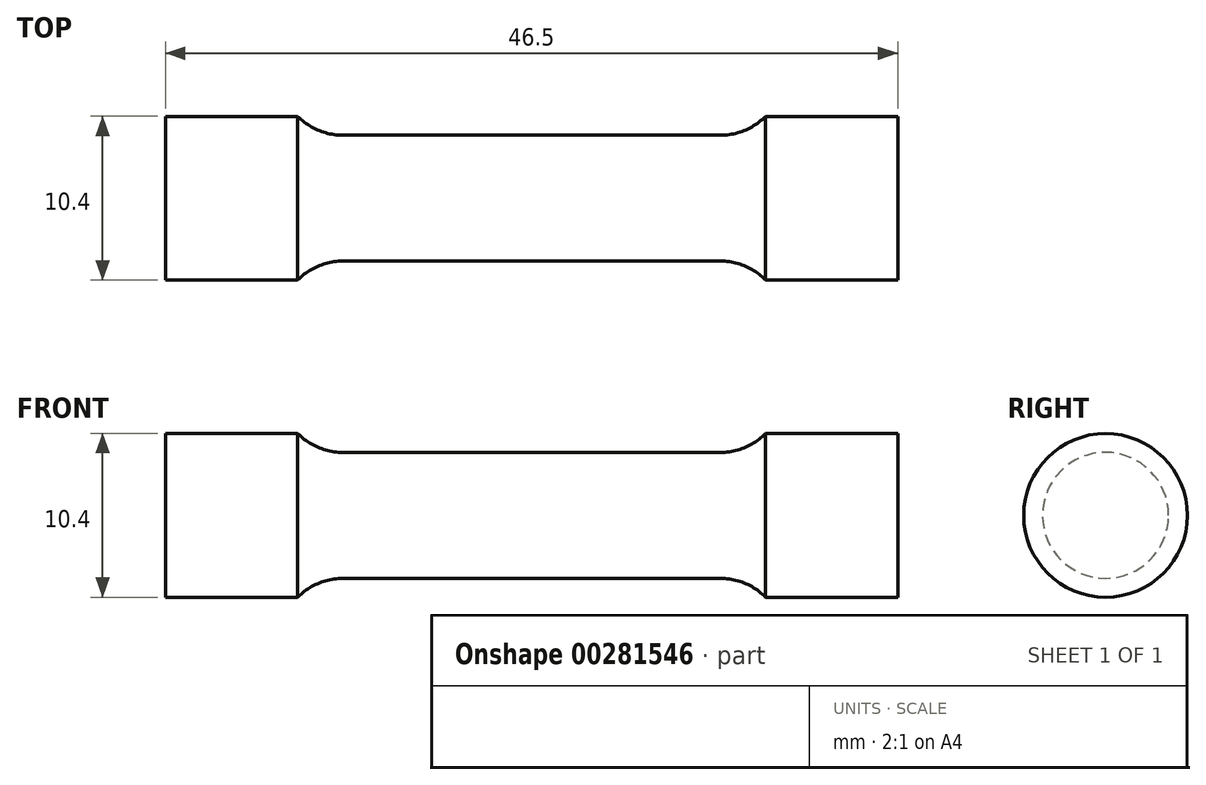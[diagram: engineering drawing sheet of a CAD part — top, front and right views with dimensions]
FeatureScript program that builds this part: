
annotation { "Feature Type Name" : "Feature", "Feature Type Description" : "" }
export const myFeature = defineFeature(function(context is Context, id is Id, definition is map)
    precondition{}
    {
        {
            var Q0;
            Q0=qCreatedBy(makeId("Front.planeOp"),FACE);
            var sketch = newSketch(context, id + "F0", { "sketchPlane" : qUnion([Q0])});
            skLineSegment(sketch, "E0", {"start": v(0, 4) * mm, "end": v(12, 4) * mm});
            skArc(sketch, "E1", {"start": v(12, 4) * mm, "mid": v(13.55, 4.31) * mm, "end": v(14.85, 5.2) * mm});
            skLineSegment(sketch, "E2", {"start": v(14.85, 5.2) * mm, "end": v(23.25, 5.2) * mm});
            skLineSegment(sketch, "E3", {"start": v(23.25, 5.2) * mm, "end": v(23.25, 0) * mm});
            skLineSegment(sketch, "E4.MirrorCS", {"start": v(0, 4) * mm, "end": v(-12, 4) * mm});
            skLineSegment(sketch, "E5.MirrorCS", {"start": v(-23.25, 5.2) * mm, "end": v(-23.25, 0) * mm});
            skLineSegment(sketch, "E6.MirrorCS", {"start": v(-14.85, 5.2) * mm, "end": v(-23.25, 5.2) * mm});
            skArc(sketch, "E7.MirrorCS", {"start": v(-12, 4) * mm, "mid": v(-13.55, 4.31) * mm, "end": v(-14.85, 5.2) * mm});
            skLineSegment(sketch, "E8", {"start": v(-23.25, 0) * mm, "end": v(23.25, 0) * mm});
            skSolve(sketch);
        }
        {
            var Q0;
            Q0 = qSketchRegion(id + "F0", true);
            var Q1;
            Q1=sQuery(id+"F0.wireOp",EDGE,"E8");
            revolve(context, id + "F1", {"entities" : qUnion([Q0]), "axis" : qUnion([Q1]), "revolveType" : RevolveType.FULL});
        }
    });
